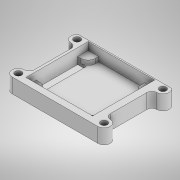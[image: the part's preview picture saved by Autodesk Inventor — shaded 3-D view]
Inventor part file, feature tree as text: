
AUTODESK INVENTOR PART (.ipt)
format: ipt  version: 2021 (Build 250183000, 183)  size: 272,384 bytes
history: native  units: mm
features: extrude x7, sketch x7, fillet x2, projected_geometry x1
ambient origin geometry x8: Origin, YZ Plane, XZ Plane, XY Plane, X Axis, Y Axis, Z Axis, Center Point
bodies: Solid1 (feature_tree)
feature tree (17):
  extrude  "Extrusion1"  Depth=25.0mm
  extrude  "Extrusion2"  Depth=2.0mm
  fillet  "Fillet1"  Radius=2.0mm
  extrude  "Extrusion3"  Depth=1.0mm TaperAngle=0.0deg
  extrude  "Extrusion4"  Depth=1.0mm
  extrude  "Extrusion5"  Depth=6.0mm
  extrude  "Extrusion6"  Depth=2.5mm
  fillet  "Fillet2"  Radius=2.0mm
  extrude  "Extrusion7"  Depth=2.0mm
  sketch  "Sketch1"  dims[d0=27.0mm d1=25.0mm]
  sketch  "Sketch2"  dims[d12=2.0mm d13=2.0mm d14=2.0mm]
  projected_geometry  "Projected Loop1"
  sketch  "Sketch4"  dims[d15=2.0mm d16=1.0mm d17=0.0mm]
  sketch  "Sketch5"  dims[d18=1.0mm d19=3.5mm]
  sketch  "Sketch6"  dims[d20=6.0mm d21=6.0mm]
  sketch  "Sketch7"  dims[d22=5.0mm d23=2.5mm d24=2.0mm]
  sketch  "Sketch8"  dims[d25=2.5mm d26=2.0mm d27=5.0mm d28=5.0mm d29=5.0mm d30=2.0mm d31=2.0mm d32=2.5mm d33=2.5mm d34=2.7mm d35=2.7mm d36=2.7mm d37=2.7mm d38=1.0mm d39=1.0mm d40=1.0mm d41=1.0mm d42=5.0mm d43=0.0mm d44=2.0mm d47=0.5mm d48=10.0mm d49=0.0mm d50=1.6mm d51=10.0mm d52=0.0mm d53=4.0mm d54=2.4mm d55=10.0mm d56=0.0mm d57=1.8mm d58=4.3mm d59=4.3mm d60=4.3mm d61=4.3mm d62=4.3mm d63=4.3mm d64=1.86mm d65=0.0mm d66=3.0mm d67=10.0mm d68=0.0mm]
